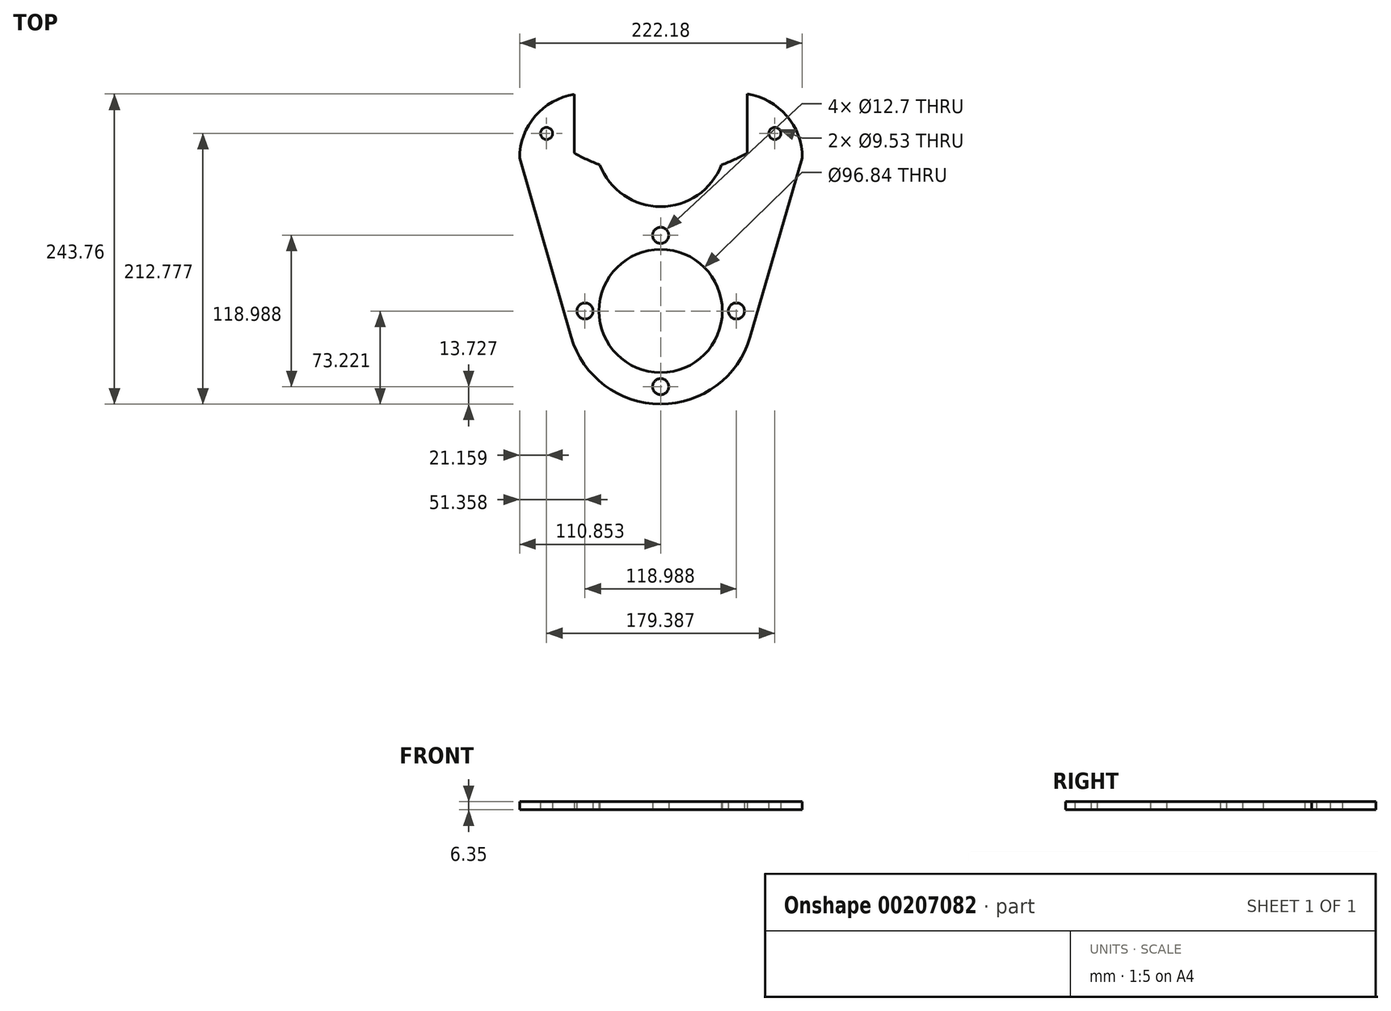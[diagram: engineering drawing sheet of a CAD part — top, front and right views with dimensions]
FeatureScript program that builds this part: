
annotation { "Feature Type Name" : "Feature", "Feature Type Description" : "" }
export const myFeature = defineFeature(function(context is Context, id is Id, definition is map)
    precondition{}
    {
        {
            var Q0;
            Q0=qCreatedBy(makeId("Top.planeOp"),FACE);
            var sketch = newSketch(context, id + "F0", { "sketchPlane" : qUnion([Q0])});
            skArc(sketch, "E0", {"start": v(-70.6, -68.96) * mm, "mid": v(-0.33, -121.88) * mm, "end": v(70.06, -69.15) * mm});
            skArc(sketch, "E1", {"start": v(-85.17, 90.9) * mm, "mid": v(-89.93, 95.66) * mm, "end": v(-94.7, 90.9) * mm});
            skArc(sketch, "E2", {"start": v(-94.7, 90.9) * mm, "mid": v(-89.93, 86.13) * mm, "end": v(-85.17, 90.9) * mm});
            skArc(sketch, "E3", {"start": v(94.22, 90.9) * mm, "mid": v(89.46, 95.66) * mm, "end": v(84.7, 90.9) * mm});
            skArc(sketch, "E4", {"start": v(84.7, 90.9) * mm, "mid": v(89.46, 86.13) * mm, "end": v(94.22, 90.9) * mm});
            skLineSegment(sketch, "E5", {"start": v(-68.1, 75.5) * mm, "end": v(-68.1, 121.58) * mm});
            skLineSegment(sketch, "E6", {"start": v(67.63, 121.88) * mm, "end": v(67.63, 75.5) * mm});
            skArc(sketch, "E7", {"start": v(-68.1, 121.58) * mm, "mid": v(-98.87, 104.42) * mm, "end": v(-111.09, 71.38) * mm});
            skArc(sketch, "E8", {"start": v(111.09, 71.62) * mm, "mid": v(98.72, 104.84) * mm, "end": v(67.63, 121.88) * mm});
            skLineSegment(sketch, "E9", {"start": v(-70.6, -68.96) * mm, "end": v(-111.09, 71.38) * mm});
            skLineSegment(sketch, "E10", {"start": v(70.06, -69.15) * mm, "end": v(111.09, 71.62) * mm});
            skArc(sketch, "E11", {"start": v(6.11, -108.15) * mm, "mid": v(-0.24, -101.8) * mm, "end": v(-6.59, -108.15) * mm});
            skArc(sketch, "E12", {"start": v(-6.59, -108.15) * mm, "mid": v(-0.24, -114.5) * mm, "end": v(6.11, -108.15) * mm});
            skArc(sketch, "E13", {"start": v(-53.38, -48.66) * mm, "mid": v(-59.73, -42.3) * mm, "end": v(-66.08, -48.66) * mm});
            skArc(sketch, "E14", {"start": v(-66.08, -48.66) * mm, "mid": v(-59.73, -55) * mm, "end": v(-53.38, -48.66) * mm});
            skArc(sketch, "E15", {"start": v(6.11, 10.84) * mm, "mid": v(-0.24, 17.19) * mm, "end": v(-6.59, 10.84) * mm});
            skArc(sketch, "E16", {"start": v(-6.59, 10.84) * mm, "mid": v(-0.24, 4.49) * mm, "end": v(6.11, 10.84) * mm});
            skArc(sketch, "E17", {"start": v(65.6, -48.66) * mm, "mid": v(59.26, -42.3) * mm, "end": v(52.9, -48.66) * mm});
            skArc(sketch, "E18", {"start": v(52.9, -48.66) * mm, "mid": v(59.26, -55) * mm, "end": v(65.6, -48.66) * mm});
            skArc(sketch, "E19", {"start": v(48.18, -48.66) * mm, "mid": v(-0.24, -0.24) * mm, "end": v(-48.66, -48.66) * mm});
            skArc(sketch, "E20", {"start": v(-48.66, -48.66) * mm, "mid": v(-0.24, -97.08) * mm, "end": v(48.18, -48.66) * mm});
            skArc(sketch, "E21", {"start": v(-48.07, 66.16) * mm, "mid": v(-0.24, 33.4) * mm, "end": v(47.6, 66.16) * mm});
            skArc(sketch, "E22", {"start": v(47.6, 66.16) * mm, "mid": v(57.8, 70.42) * mm, "end": v(67.63, 75.5) * mm});
            skArc(sketch, "E23", {"start": v(-68.1, 75.5) * mm, "mid": v(-58.27, 70.42) * mm, "end": v(-48.07, 66.16) * mm});
            skSolve(sketch);
        }
        {
            var Q0;
            Q0=makeQuery(id+"F0.imprint","IMPRINT",FACE,{"disambiguationData":[TD([[makeQuery(id+"F0.imprint","IMPRINT",EDGE,{"derivedFrom":sQuery(id+"F0.wireOp",EDGE,"E0")}),1.0]])]});
            extrude(context, id + "F1", {"entities" : qUnion([Q0]), "depth" : 6.35 * mm});
        }
    });
